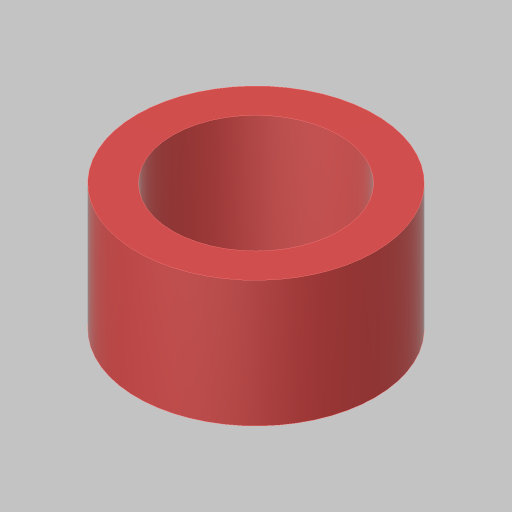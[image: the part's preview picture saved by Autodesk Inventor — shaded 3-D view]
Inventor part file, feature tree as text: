
AUTODESK INVENTOR PART (.ipt)
format: ipt  version: 2023.5 (Build 275446000, 446)  size: 104,960 bytes
history: native  units: in
note: dims shown in document units (in); Inventor stores cm internally (conversion verified against a paired STEP export)
features: extrude x1, sketch x1
ambient origin geometry x8: Origin, YZ Plane, XZ Plane, XY Plane, X Axis, Y Axis, Z Axis, Center Point
bodies: Solid1 (feature_tree)
feature tree (2):
  extrude  "Extrusion1"  Depth=0.44in
  sketch  "Sketch1"  dims[d0=0.58in d1=0.125in d2=0.44in d3=0.0in]
